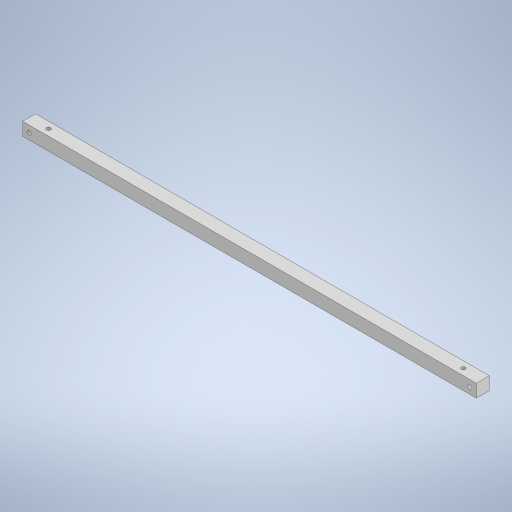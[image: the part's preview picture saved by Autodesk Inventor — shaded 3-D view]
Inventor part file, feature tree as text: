
AUTODESK INVENTOR PART (.ipt)
format: ipt  version: 2023 (Build 270158000, 158)  size: 252,416 bytes
history: native  units: mm
features: sketch x3, hole x2, other x1, extrude x1
ambient origin geometry x8: Origin, YZ Plane, XZ Plane, XY Plane, X Axis, Y Axis, Z Axis, Center Point
bodies: Body1 (feature_tree)
feature tree (7):
  other  "ソリッド1"
  extrude  "押し出し1"  Depth=350.0mm
  hole  "穴1"  [1 undecoded]
  hole  "穴2"  [1 undecoded]
  sketch  "スケッチ1"
  sketch  "スケッチ2"
  sketch  "スケッチ3"
note: 2 required parameter values undecoded (feature->parameter linkage not recoverable at this tier; creation-order binding heuristic only, values carry confidence <= 0.55)
